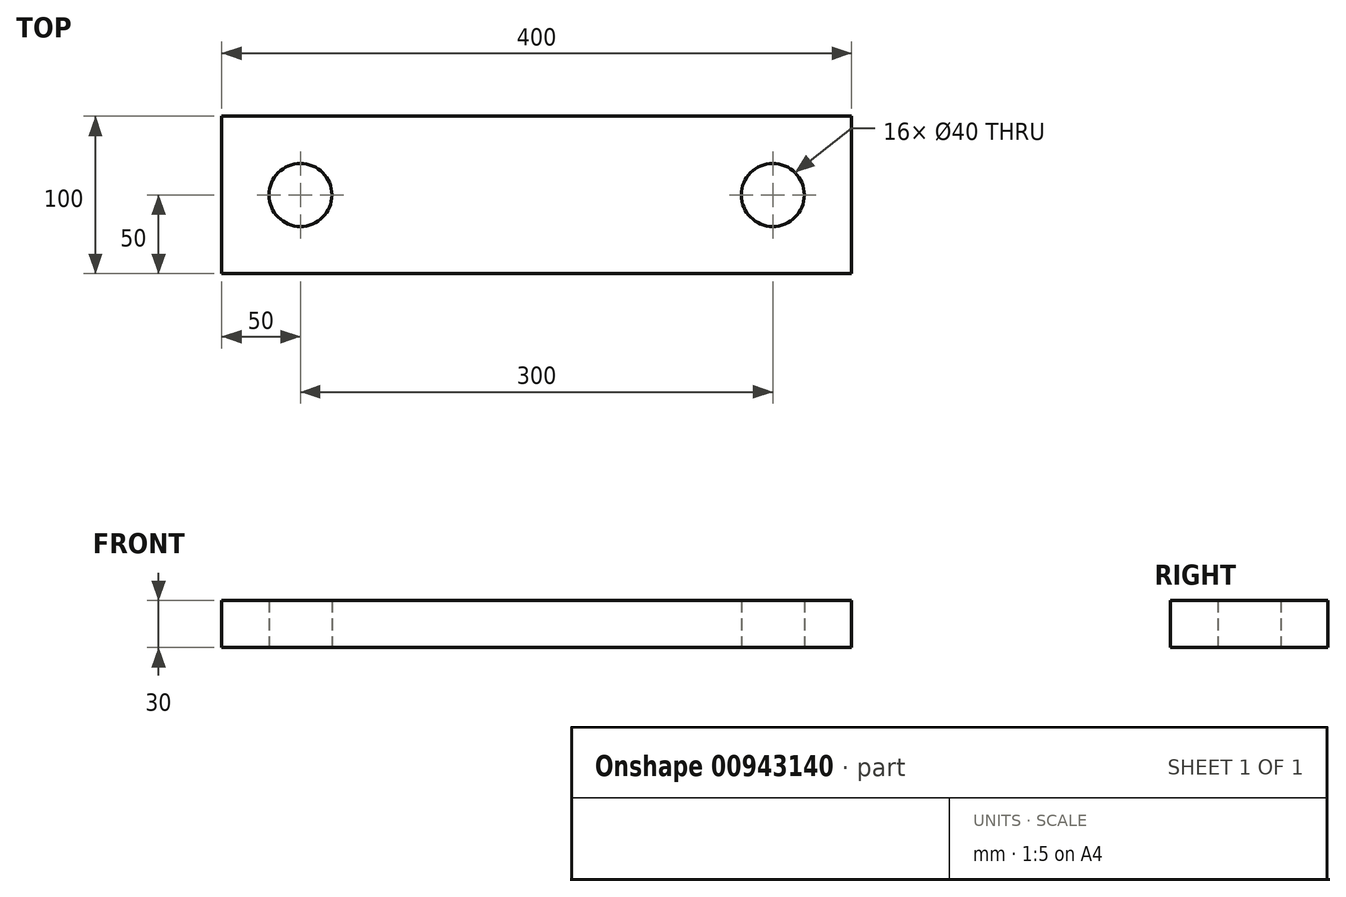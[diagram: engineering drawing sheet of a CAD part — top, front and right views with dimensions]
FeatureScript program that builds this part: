
annotation { "Feature Type Name" : "Feature", "Feature Type Description" : "" }
export const myFeature = defineFeature(function(context is Context, id is Id, definition is map)
    precondition{}
    {
        {
            var Q0;
            Q0=qCreatedBy(makeId("Top.planeOp"),FACE);
            var sketch = newSketch(context, id + "F0", { "sketchPlane" : qUnion([Q0])});
            skLineSegment(sketch, "E0.bottom", {"start": v(0, 0) * mm, "end": v(400, 0) * mm});
            skLineSegment(sketch, "E0.top", {"start": v(0, -100) * mm, "end": v(400, -100) * mm});
            skLineSegment(sketch, "E0.left", {"start": v(0, 0) * mm, "end": v(0, -100) * mm});
            skLineSegment(sketch, "E0.right", {"start": v(400, 0) * mm, "end": v(400, -100) * mm});
            skPoint(sketch, "E1", {"position": v(50, -50) * mm});
            skPoint(sketch, "E2", {"position": v(350, -50) * mm});
            skCircle(sketch, "E3", {"center": v(50, -50) * mm, "radius": 20 * mm});
            skCircle(sketch, "E4", {"center": v(350, -50) * mm, "radius": 20 * mm});
            skSolve(sketch);
        }
        {
            var Q0;
            Q0=makeQuery(id+"F0.imprint","IMPRINT",FACE,{"disambiguationData":[TD([[makeQuery(id+"F0.imprint","IMPRINT",EDGE,{"derivedFrom":sQuery(id+"F0.wireOp",EDGE,"E0.bottom")}),-1.0]])]});
            extrude(context, id + "F1", {"entities" : qUnion([Q0]), "depth" : 30 * mm, "offsetDistance" : 25 * mm});
        }
    });
